# Revit family: HL_Трап для балконов и террас_HL80HR
name_source: partatom
category: Instalační zařizovací předměty
revit_build: Autodesk Revit 2016 (Build: 20151007_0715(x64)
units: mm (PartAtom-declared; Revit-internal decimal feet)

## family parameters
Bod výpočtu místnosti = Ano
Kóta kulaté spojky = Použít průměr
Nadpis OmniClass = Deck Waste Water Drains
Ořezat dutým tvarem při načtení = Ne
Sdílené = Ne
Typ součásti = Normální
Vždy vertikální = Ano
Založené na pracovní rovině = Ne
Číslo OmniClass = 23.70.50.21.24.14

## types (1)
- HL_Трап для балконов и террас_HL80HR
    EAN = 9003076010868
    Klíčová poznámka = HL80HR
    Komentáře k typům = Трап для балконов и террас DN50/75 поворотный с битумным полотном, с морозоустойчивой запахозапирающей заслонкой и с круглой насадкой d 131мм/d 112мм.
    Model = HL80HR
    Popis = Трап для балконов и террас
    Připojení CW = Ne
    Připojení HW = Ne
    Připojení odpadu = Ano
    Připojení ventilace = Ne
    URL = http://www.hutterer-lechner.com
    Výrobce = HL Hutterer & Lechner GmbH
    ВЕС = 1,34 kg
    ВЫСОТА МОНТАЖА = 115mm
    МАКСИМАЛЬНАЯ НАГРУЗКА КЛАССА = K3 -300kg
    МАТЕРИАЛ = PP / PE
    НАСАДКА = 20-73mm/d 131mm
    ПРОИЗВОДИТЕЛЬНОСТЬ = 0,80 l/s
    РАЗМЕР = DN50/75
    РЕШЁТКА = Edelstahl rund d 112mm

## geometry (parser evidence)
native form markers: Blend x12, Sweep x31
no freeform markers — native parametric forms only
